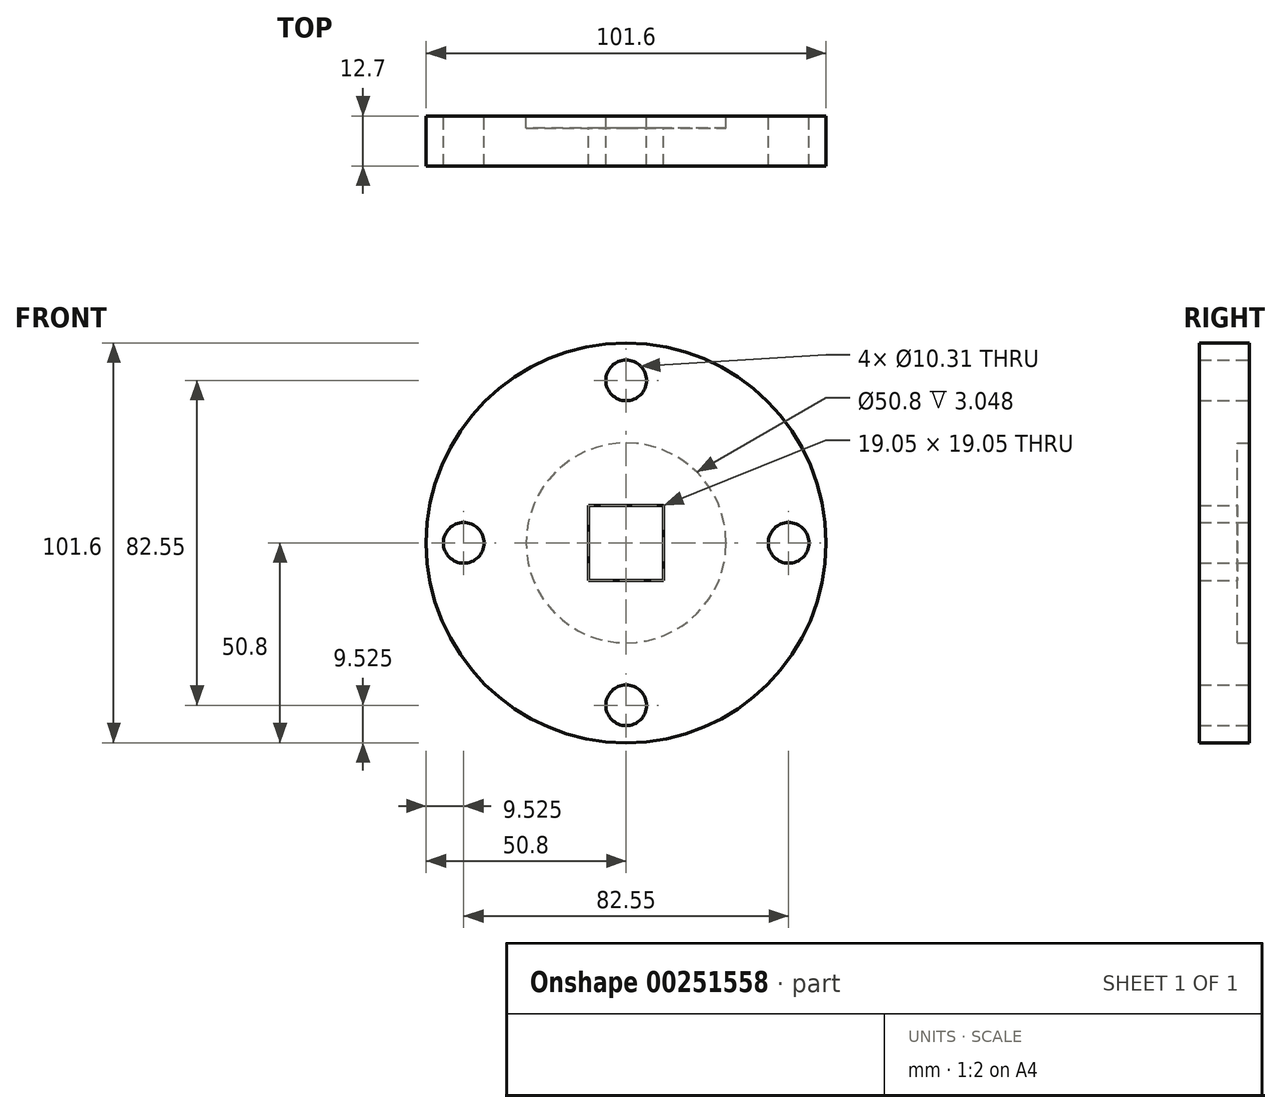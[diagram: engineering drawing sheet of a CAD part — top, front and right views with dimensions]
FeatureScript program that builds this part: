
annotation { "Feature Type Name" : "Feature", "Feature Type Description" : "" }
export const myFeature = defineFeature(function(context is Context, id is Id, definition is map)
    precondition{}
    {
        {
            var Q0;
            Q0=qCreatedBy(makeId("Front.planeOp"),FACE);
            var sketch = newSketch(context, id + "F0", { "sketchPlane" : qUnion([Q0])});
            skCircle(sketch, "E0", {"center": v(0, 0) * mm, "radius": 50.8 * mm});
            skLineSegment(sketch, "E1.bottom", {"start": v(9.53, 9.53) * mm, "end": v(-9.52, 9.53) * mm});
            skLineSegment(sketch, "E1.top", {"start": v(9.53, -9.53) * mm, "end": v(-9.53, -9.53) * mm});
            skLineSegment(sketch, "E1.left", {"start": v(9.53, 9.53) * mm, "end": v(9.53, -9.53) * mm});
            skLineSegment(sketch, "E1.right", {"start": v(-9.53, 9.53) * mm, "end": v(-9.53, -9.53) * mm});
            skCircle(sketch, "E2", {"center": v(-41.28, 0) * mm, "radius": 5.16 * mm});
            skCircle(sketch, "E3", {"center": v(0, 41.28) * mm, "radius": 5.16 * mm});
            skCircle(sketch, "E4", {"center": v(41.28, 0) * mm, "radius": 5.16 * mm});
            skCircle(sketch, "E5", {"center": v(0, -41.28) * mm, "radius": 5.16 * mm});
            skSolve(sketch);
        }
        {
            var Q0;
            Q0=makeQuery(id+"F0.imprint","IMPRINT",FACE,{"disambiguationData":[TD([[makeQuery(id+"F0.imprint","IMPRINT",EDGE,{"derivedFrom":sQuery(id+"F0.wireOp",EDGE,"E0")}),1.0]])]});
            extrude(context, id + "F1", {"entities" : qUnion([Q0]), "depth" : 12.7 * mm});
        }
        {
            var Q0;
            Q0=qCreatedBy(makeId("Front.planeOp"),FACE);
            var sketch = newSketch(context, id + "F2", { "sketchPlane" : qUnion([Q0])});
            skCircle(sketch, "E6", {"center": v(0, 0) * mm, "radius": 25.4 * mm});
            skSolve(sketch);
        }
        {
            var Q0;
            Q0 = qSketchRegion(id + "F2", true);
            extrude(context, id + "F3", {"entities" : qUnion([Q0]), "operationType" : NewBodyOperationType.REMOVE, "depth" : 3.05 * mm});
        }
    });
